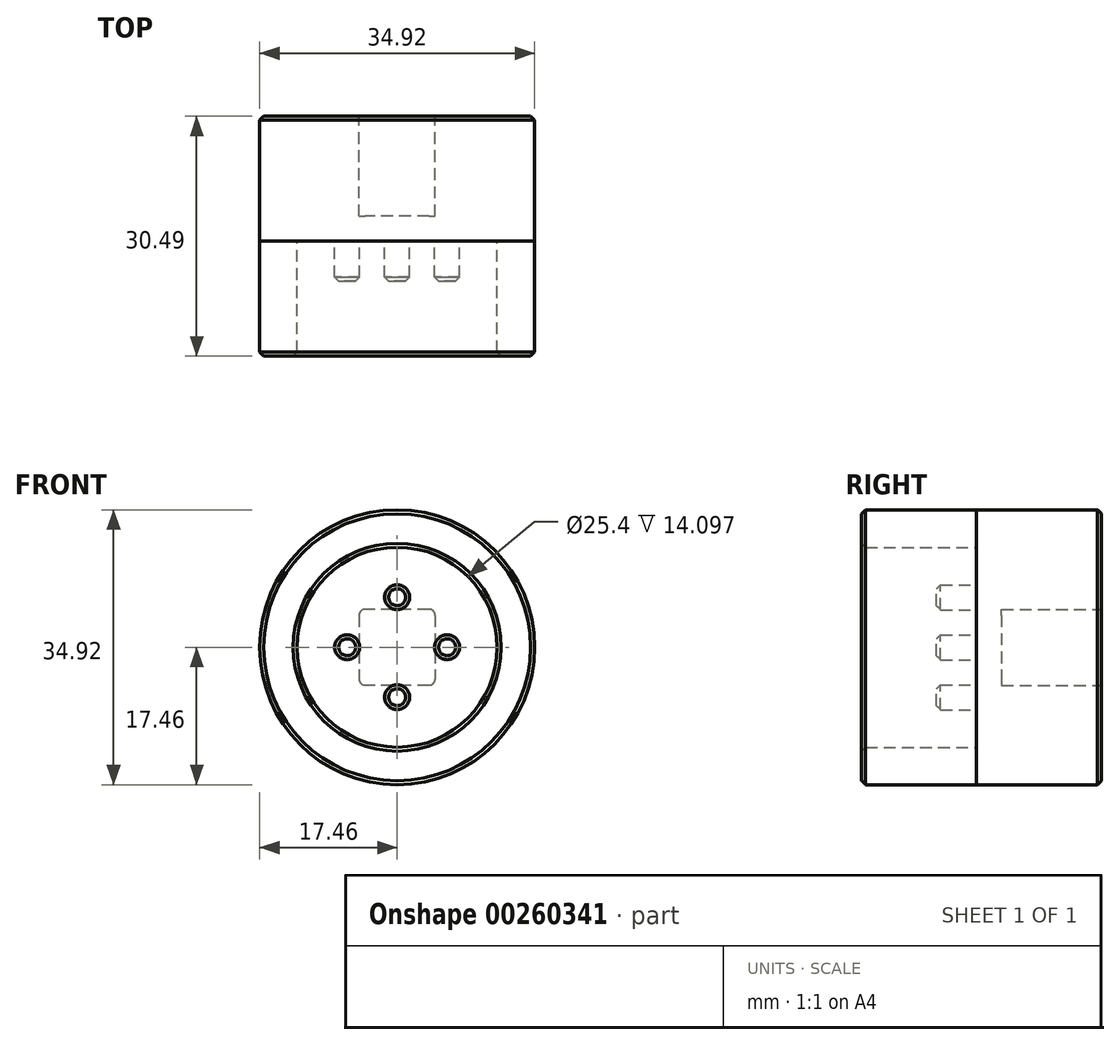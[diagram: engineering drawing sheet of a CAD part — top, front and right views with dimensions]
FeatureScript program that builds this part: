
annotation { "Feature Type Name" : "Feature", "Feature Type Description" : "" }
export const myFeature = defineFeature(function(context is Context, id is Id, definition is map)
    precondition{}
    {
        {
            var Q0;
            Q0=qCreatedBy(makeId("Front.planeOp"),FACE);
            var sketch = newSketch(context, id + "F0", { "sketchPlane" : qUnion([Q0])});
            skCircle(sketch, "E0", {"center": v(0, 0) * mm, "radius": 12.7 * mm});
            skCircle(sketch, "E1", {"center": v(0, 0) * mm, "radius": 17.46 * mm});
            skCircle(sketch, "E2", {"center": v(0, 6.35) * mm, "radius": 1.59 * mm});
            skCircle(sketch, "E3.1.0", {"center": v(-6.35, 0) * mm, "radius": 1.59 * mm});
            skCircle(sketch, "E3.2.0", {"center": v(0, -6.35) * mm, "radius": 1.59 * mm});
            skCircle(sketch, "E3.3.0", {"center": v(6.35, 0) * mm, "radius": 1.59 * mm});
            skSolve(sketch);
        }
        {
            var Q0;
            Q0 = qSketchRegion(id + "F0", true);
            var Q1;
            Q1=makeQuery(id+"F0.imprint","IMPRINT",FACE,{"disambiguationData":[TD([[makeQuery(id+"F0.imprint","IMPRINT",EDGE,{"derivedFrom":sQuery(id+"F0.wireOp",EDGE,"E2")}),1.0]])]});
            var Q2;
            Q2=makeQuery(id+"F0.imprint","IMPRINT",FACE,{"disambiguationData":[TD([[makeQuery(id+"F0.imprint","IMPRINT",EDGE,{"derivedFrom":sQuery(id+"F0.wireOp",EDGE,"E3.3.0")}),1.0]])]});
            var Q3;
            Q3=makeQuery(id+"F0.imprint","IMPRINT",FACE,{"disambiguationData":[TD([[makeQuery(id+"F0.imprint","IMPRINT",EDGE,{"derivedFrom":sQuery(id+"F0.wireOp",EDGE,"E3.2.0")}),1.0]])]});
            var Q4;
            Q4=makeQuery(id+"F0.imprint","IMPRINT",FACE,{"disambiguationData":[TD([[makeQuery(id+"F0.imprint","IMPRINT",EDGE,{"derivedFrom":sQuery(id+"F0.wireOp",EDGE,"E3.1.0")}),1.0]])]});
            extrude(context, id + "F1", {"entities" : qUnion([Q0, Q1, Q2, Q3, Q4]), "depth" : 5.08 * mm});
        }
        {
            var Q0;
            Q0=makeQuery(id+"F1.opExtrude","CAP_FACE",FACE,{"disambiguationData":[OSD([sQuery(id+"F0.wireOp",EDGE,"E0"),sQuery(id+"F0.wireOp",EDGE,"E1")])],"isStart":true});
            var sketch = newSketch(context, id + "F2", { "sketchPlane" : qUnion([Q0])});
            skCircle(sketch, "E4", {"center": v(0, 0) * mm, "radius": 17.46 * mm});
            skSolve(sketch);
        }
        {
            var Q0;
            Q0 = qSketchRegion(id + "F2", true);
            extrude(context, id + "F3", {"entities" : qUnion([Q0]), "depth" : 9.52 * mm});
        }
        {
            var Q0;
            Q0=makeQuery(id+"F1.opExtrude","CAP_FACE",FACE,{"disambiguationData":[OSD([sQuery(id+"F0.wireOp",EDGE,"E0"),sQuery(id+"F0.wireOp",EDGE,"E1")])],"isStart":false});
            extrude(context, id + "F4", {"entities" : qUnion([Q0]), "operationType" : NewBodyOperationType.ADD, "depth" : 9.52 * mm});
        }
        {
            var Q0;
            Q0=makeQuery(id+"F3.opExtrude","CAP_FACE",FACE,{"disambiguationData":[OSD([sQuery(id+"F2.wireOp",EDGE,"E4")])],"isStart":false});
            extrude(context, id + "F5", {"entities" : qUnion([Q0]), "operationType" : NewBodyOperationType.ADD, "depth" : 6.35 * mm});
        }
        {
            var Q0;
            Q0=makeQuery(id+"F5.opExtrude","CAP_FACE",FACE,{"disambiguationData":[OSD([sQuery(id+"F2.wireOp",EDGE,"E4")])],"isStart":false});
            var sketch = newSketch(context, id + "F6", { "sketchPlane" : qUnion([Q0])});
            skLineSegment(sketch, "E5.bottom", {"start": v(-4.83, 4.83) * mm, "end": v(4.83, 4.83) * mm});
            skLineSegment(sketch, "E5.top", {"start": v(-4.83, -4.83) * mm, "end": v(4.83, -4.83) * mm});
            skLineSegment(sketch, "E5.left", {"start": v(-4.83, 4.83) * mm, "end": v(-4.83, -4.83) * mm});
            skLineSegment(sketch, "E5.right", {"start": v(4.83, 4.83) * mm, "end": v(4.83, -4.83) * mm});
            skPoint(sketch, "E5.middle", {"position": v(0, 0) * mm});
            skSolve(sketch);
        }
        {
            var Q0;
            Q0 = qSketchRegion(id + "F6", true);
            extrude(context, id + "F7", {"entities" : qUnion([Q0]), "operationType" : NewBodyOperationType.REMOVE, "oppositeDirection" : true, "depth" : 12.7 * mm});
        }
        {
            var Q0;
            Q0=makeQuery(id+"F7.boolean.opBoolean","COPY",EDGE,{"derivedFrom":makeQuery(id+"F7.opExtrude","SWEPT_EDGE",EDGE,{"disambiguationData":[OSD([sQuery(id+"F6.wireOp",EDGE,"E5.bottom"),sQuery(id+"F6.wireOp",EDGE,"E5.left")])]})});
            var Q1;
            Q1=makeQuery(id+"F7.boolean.opBoolean","COPY",EDGE,{"derivedFrom":makeQuery(id+"F7.opExtrude","SWEPT_EDGE",EDGE,{"disambiguationData":[OSD([sQuery(id+"F6.wireOp",EDGE,"E5.top"),sQuery(id+"F6.wireOp",EDGE,"E5.left")])]})});
            var Q2;
            Q2=makeQuery(id+"F7.boolean.opBoolean","COPY",EDGE,{"derivedFrom":makeQuery(id+"F7.opExtrude","SWEPT_EDGE",EDGE,{"disambiguationData":[OSD([sQuery(id+"F6.wireOp",EDGE,"E5.top"),sQuery(id+"F6.wireOp",EDGE,"E5.right")])]})});
            var Q3;
            Q3=makeQuery(id+"F7.boolean.opBoolean","COPY",EDGE,{"derivedFrom":makeQuery(id+"F7.opExtrude","SWEPT_EDGE",EDGE,{"disambiguationData":[OSD([sQuery(id+"F6.wireOp",EDGE,"E5.bottom"),sQuery(id+"F6.wireOp",EDGE,"E5.right")])]})});
            fillet(context, id + "F8", {"entities" : qUnion([Q0, Q1, Q2, Q3]), "radius" : 0.76 * mm, "tangentPropagation" : true, "allowEdgeOverflow" : false});
        }
        {
            var Q0;
            Q0=makeQuery(id+"F7.boolean.opBoolean","COPY",EDGE,{"derivedFrom":makeQuery(id+"F7.opExtrude","CAP_EDGE",EDGE,{"disambiguationData":[OSD([sQuery(id+"F6.wireOp",EDGE,"E5.bottom")])],"isStart":true})});
            var Q1;
            Q1=makeQuery(id+"F5.opExtrude","CAP_EDGE",EDGE,{"disambiguationData":[OSD([sQuery(id+"F2.wireOp",EDGE,"E4")])],"isStart":false});
            var Q2;
            Q2=makeQuery(id+"F4.opExtrude","CAP_EDGE",EDGE,{"disambiguationData":[OSD([sQuery(id+"F0.wireOp",EDGE,"E1")])],"isStart":false});
            var Q3;
            Q3=makeQuery(id+"F4.opExtrude","CAP_EDGE",EDGE,{"disambiguationData":[OSD([sQuery(id+"F0.wireOp",EDGE,"E0")])],"isStart":false});
            var Q4;
            Q4=makeQuery(id+"F1.opExtrude","CAP_EDGE",EDGE,{"disambiguationData":[OSD([sQuery(id+"F0.wireOp",EDGE,"E3.2.0")])],"isStart":false});
            var Q5;
            Q5=makeQuery(id+"F1.opExtrude","CAP_EDGE",EDGE,{"disambiguationData":[OSD([sQuery(id+"F0.wireOp",EDGE,"E3.3.0")])],"isStart":false});
            var Q6;
            Q6=makeQuery(id+"F1.opExtrude","CAP_EDGE",EDGE,{"disambiguationData":[OSD([sQuery(id+"F0.wireOp",EDGE,"E2")])],"isStart":false});
            var Q7;
            Q7=makeQuery(id+"F1.opExtrude","CAP_EDGE",EDGE,{"disambiguationData":[OSD([sQuery(id+"F0.wireOp",EDGE,"E3.1.0")])],"isStart":false});
            chamfer(context, id + "F9", {"entities" : qUnion([Q0, Q1, Q2, Q3, Q4, Q5, Q6, Q7]), "width" : 0.5 * mm, "tangentPropagation" : true});
        }
    });
